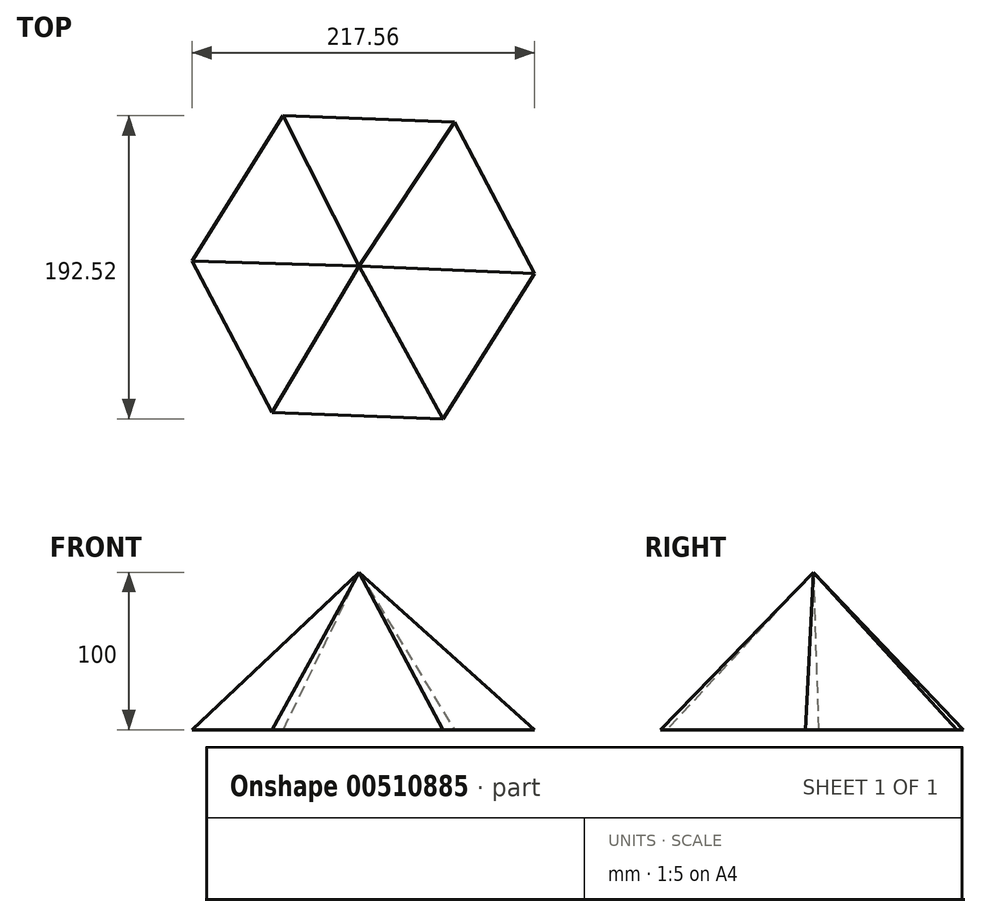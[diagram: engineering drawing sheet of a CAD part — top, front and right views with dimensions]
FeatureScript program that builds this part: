
annotation { "Feature Type Name" : "Feature", "Feature Type Description" : "" }
export const myFeature = defineFeature(function(context is Context, id is Id, definition is map)
    precondition{}
    {
        {
            var Q0;
            Q0=qCreatedBy(makeId("Top.planeOp"),FACE);
            var sketch = newSketch(context, id + "F0", { "sketchPlane" : qUnion([Q0])});
            skCircle(sketch, "E0.cCircle", {"center": v(0, 0) * mm, "radius": 108.85 * mm, "construction": true});
            skLineSegment(sketch, "E0.0", {"start": v(-57.94, -92.15) * mm, "end": v(-108.78, 4.1) * mm});
            skLineSegment(sketch, "E0.1", {"start": v(-108.78, 4.1) * mm, "end": v(-50.83, 96.26) * mm});
            skLineSegment(sketch, "E0.2", {"start": v(-50.83, 96.26) * mm, "end": v(57.94, 92.15) * mm});
            skLineSegment(sketch, "E0.3", {"start": v(57.94, 92.15) * mm, "end": v(108.78, -4.1) * mm});
            skLineSegment(sketch, "E0.4", {"start": v(108.78, -4.1) * mm, "end": v(50.83, -96.26) * mm});
            skLineSegment(sketch, "E0.5", {"start": v(50.83, -96.26) * mm, "end": v(-57.94, -92.15) * mm});
            skSolve(sketch);
        }
        {
            var Q0;
            Q0=qCreatedBy(makeId("Top.planeOp"),FACE);
            var Q1;
            Q1=qBodyType(qCreatedBy(id+"F2",EDGE),BodyType.WIRE);
            cPlane(context, id + "F1", {"entities" : qUnion([Q0, Q1]), "cplaneType" : CPlaneType.OFFSET, "offset" : 100 * mm, "width" : 150 * mm, "height" : 150 * mm});
        }
        {
            var Q0;
            Q0=qCreatedBy(id+"F1.planeOp",FACE);
            var sketch = newSketch(context, id + "F2", { "sketchPlane" : qUnion([Q0])});
            skPoint(sketch, "E1", {"position": v(-2.55, 0.86) * mm});
            skSolve(sketch);
        }
        {
            var Q0;
            Q0=sQuery(id+"F2.wireOp",VERTEX,"E1");
            var Q1;
            Q1=makeQuery(id+"F0.imprint","IMPRINT",FACE,{"disambiguationData":[TD([[makeQuery(id+"F0.imprint","IMPRINT",EDGE,{"derivedFrom":sQuery(id+"F0.wireOp",EDGE,"E0.0")}),-1.0]])]});
            loft(context, id + "F3", {"sheetProfilesArray" : [{ "sheetProfileEntities" : qUnion([Q0]) }, { "sheetProfileEntities" : qUnion([Q1]) }]});
        }
    });
